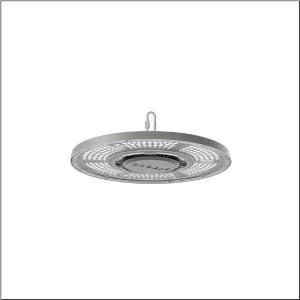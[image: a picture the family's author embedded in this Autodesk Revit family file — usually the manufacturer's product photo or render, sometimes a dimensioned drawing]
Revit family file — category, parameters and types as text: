
# Revit family: highbay_31-s_51hc41da4fmb
name_source: partatom
category: Lighting Fixtures
units: mm (PartAtom-declared; Revit-internal decimal feet)

## family parameters
Cut with Voids When Loaded = No
Host = Face
Light Source = No
Part Type = Normal
Room Calculation Point = No
Round Connector Dimension = Use Diameter
Shared = No

## types (1)
- Highbay 31-S (1 x LED, 14000 lm, 94 W, 4000K)
    Apparent Load = 94 VA
    CIE Flux Codes = 94 98 100 100 100
    Color Rendering = 80
    Color Temperature = 4000K
    Default Elevation = 1800 mm
    Description = Highbay 31-S, LED high bay luminaire, primary light control with lens, of PC, primary optical cover: cover panel, of PC, transparent, light emission: direct distribution, primary light characteristic: rotationally symmetric, installation type: suspended mounting, surface-mounted, LED, rated luminous flux: 14.000lm, luminous efficacy: 150lm/W, light colour: 840, colour temperature: 4000K, control gear: ECG DALI, with cable, 5x 1.0mm², free wire ends, mains connection: 220..240V, AC/DC, 0/50..60Hz, cable length: 1,5m, rated input power: 94W, housing, rotationally symmetric, of diecast aluminium, powder-coated, grey aluminium (RAL 9007), with hook on luminaire side, incl. screw, diameter: 339mm, protection rating (complete): IP65, insulation class (complete): insulation class I (protective earthing), certification: CE, ENEC, UKCA, protection symbol: D, impact resistance: IK08, permissible operating ambient temperature: -30..+45°C, standard: EN 60598-2-22, EN 60598, corresponds to IFS (International Featured Standards) requirements for safety and quality in the food industry, packaging unit: 1 piece
    Height = 141 mm
    Lamp = 1 x LED
    Lamp Light Flux = 14000 lm
    Lamp Power = 94 W
    Lamp count = 1
    Length = 339 mm
    Luminous efficacy = 149 lm/W
    Manufacturer = Siteco
    ModVariant = No
    Model = 51HC41DA4FMB
    Mounting Place = Ceiling
    Mounting Type = Pendant
    Number of Poles = 1
    OnlyDefault = Yes
    Power Factor = 1
    Product Name = Highbay 31-S
    Product group = LED high bay luminaire
    ProductGroupID = 903
    Protection Class = Protection class I
    Protection Degree = IP 65
    RLX_Detail_Level = 1
    RLX_Emergency_Light_Flux = 0 lm
    RLX_Emergency_Type = 0
    RLX_Emergency_Type_DB = No
    RlxData = <blob elided: 107941 chars, md5=f0e56c84>
    Socket = socket
    Standby Power = 0 W
    System Light Flux = 14000 lm
    System Power = 94 W
    Type Comments = Product without accessories
    Type Image = l_1007237.jpg
    URL = http://relux.com
    VarID = ---
    Voltage = 0 V
    Weight = 0.00 kg
    Width = 0 mm  [stored 0 ft]

note: [stored X ft] marks values corroborated as IEEE doubles in the binary element streams (Revit-internal decimal feet)

## geometry (parser evidence)
native form markers: Blend x4, Sweep x9
no freeform markers — native parametric forms only
